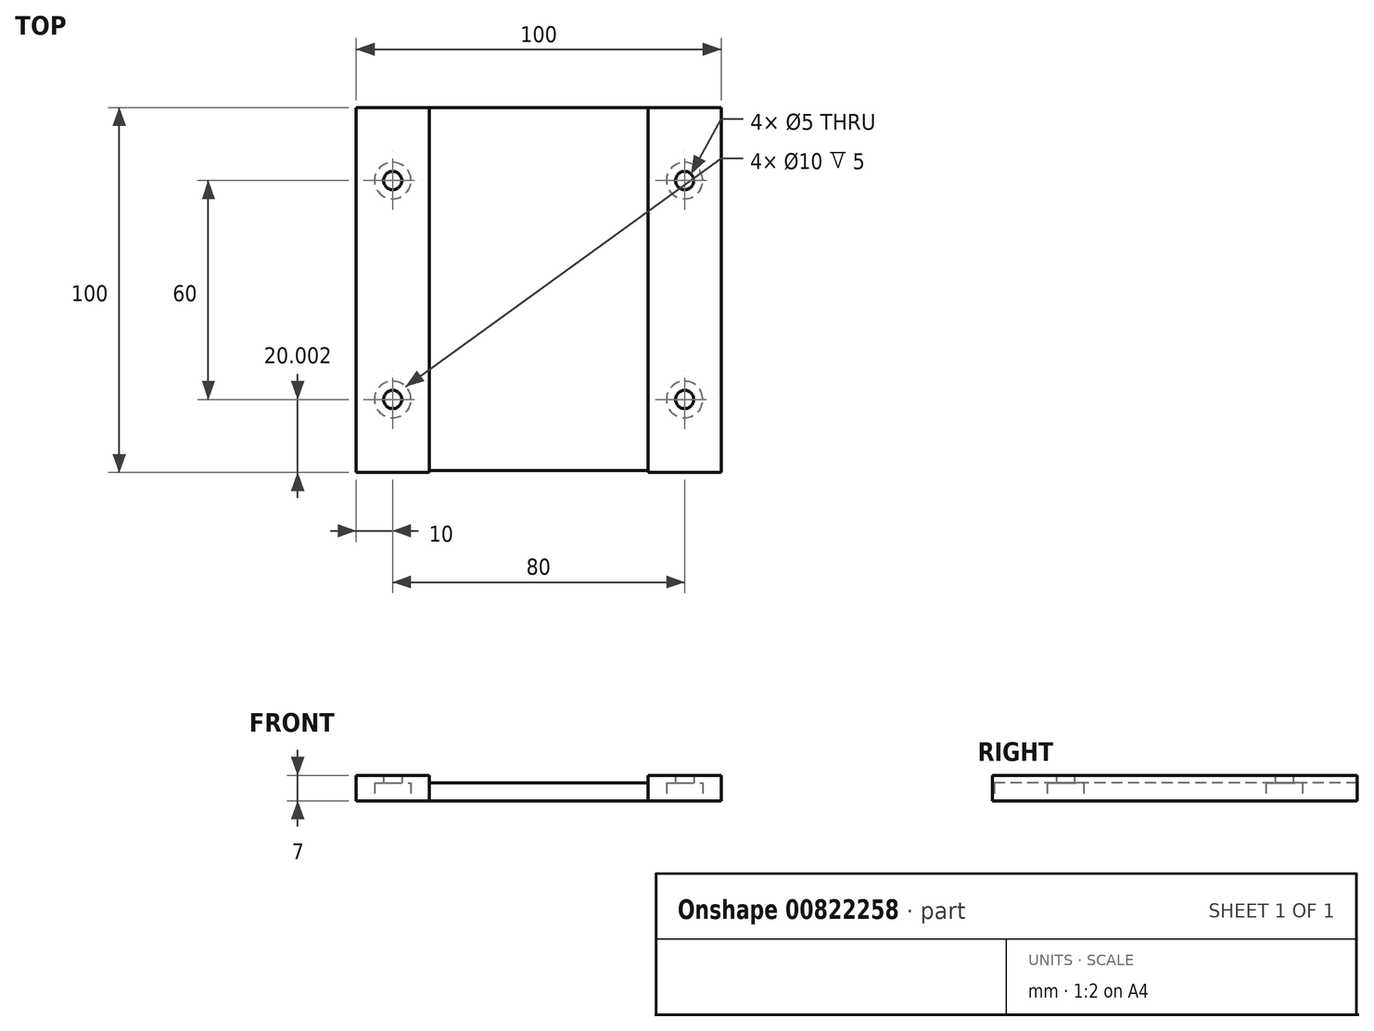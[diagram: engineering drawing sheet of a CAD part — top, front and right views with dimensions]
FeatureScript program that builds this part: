
annotation { "Feature Type Name" : "Feature", "Feature Type Description" : "" }
export const myFeature = defineFeature(function(context is Context, id is Id, definition is map)
    precondition{}
    {
        {
            var Q0;
            Q0=qCreatedBy(makeId("Top.planeOp"),FACE);
            var sketch = newSketch(context, id + "F0", { "sketchPlane" : qUnion([Q0])});
            skLineSegment(sketch, "E0.bottom", {"start": v(-50, 49.93) * mm, "end": v(-30, 49.93) * mm});
            skLineSegment(sketch, "E0.top", {"start": v(-50, -50.07) * mm, "end": v(-30, -50.07) * mm});
            skLineSegment(sketch, "E0.left", {"start": v(-50, 49.93) * mm, "end": v(-50, -50.07) * mm});
            skLineSegment(sketch, "E0.right", {"start": v(-30, 49.93) * mm, "end": v(-30, -50.07) * mm});
            skLineSegment(sketch, "E1.bottom", {"start": v(-30, 49.93) * mm, "end": v(30, 49.93) * mm});
            skLineSegment(sketch, "E1.top", {"start": v(-30, -49.53) * mm, "end": v(30, -49.53) * mm});
            skLineSegment(sketch, "E1.left", {"start": v(-30, 49.93) * mm, "end": v(-30, -49.53) * mm});
            skLineSegment(sketch, "E1.right", {"start": v(30, 49.93) * mm, "end": v(30, -49.53) * mm});
            skLineSegment(sketch, "E2.bottom", {"start": v(30, 49.93) * mm, "end": v(50, 49.93) * mm});
            skLineSegment(sketch, "E2.top", {"start": v(30, -50.07) * mm, "end": v(50, -50.07) * mm});
            skLineSegment(sketch, "E2.left", {"start": v(30, 49.93) * mm, "end": v(30, -50.07) * mm});
            skLineSegment(sketch, "E2.right", {"start": v(50, 49.93) * mm, "end": v(50, -50.07) * mm});
            skPoint(sketch, "E3", {"position": v(-40, 29.93) * mm});
            skPoint(sketch, "E4", {"position": v(-40, -30.07) * mm});
            skPoint(sketch, "E5.MirrorP", {"position": v(40, 29.93) * mm});
            skPoint(sketch, "E6.MirrorP", {"position": v(40, -30.07) * mm});
            skSolve(sketch);
        }
        {
            var Q0;
            {var subQ0=sQuery(id+"F0.wireOp",EDGE,"E1.bottom");Q0=makeQuery(id+"F0.imprint","IMPRINT",FACE,{"disambiguationData":[TD([[makeQuery(id+"F0.imprint","IMPRINT",EDGE,{"derivedFrom":subQ0}),-1.0]])]});}
            extrude(context, id + "F1", {"entities" : qUnion([Q0]), "depth" : 5 * mm, "offsetDistance" : 25 * mm});
        }
        {
            var Q0;
            Q0=makeQuery(id+"F0.imprint","IMPRINT",FACE,{"disambiguationData":[TD([[makeQuery(id+"F0.imprint","IMPRINT",EDGE,{"derivedFrom":sQuery(id+"F0.wireOp",EDGE,"E0.bottom")}),-1.0]])]});
            var Q1;
            {var subQ3=sQuery(id+"F0.wireOp",EDGE,"E2.bottom");Q1=makeQuery(id+"F0.imprint","IMPRINT",FACE,{"disambiguationData":[TD([[makeQuery(id+"F0.imprint","IMPRINT",EDGE,{"derivedFrom":subQ3}),-1.0]])]});}
            extrude(context, id + "F2", {"entities" : qUnion([Q0, Q1]), "operationType" : NewBodyOperationType.ADD, "depth" : 7 * mm, "offsetDistance" : 25 * mm, "hasSecondDirection" : true, "secondDirectionOppositeDirection" : true, "secondDirectionDepth" : 0 * mm});
        }
        {
            var Q0;
            Q0=sQuery(id+"F0.wireOp",VERTEX,"E4");
            var Q1;
            Q1=sQuery(id+"F0.wireOp",VERTEX,"E3");
            var Q2;
            Q2=sQuery(id+"F0.wireOp",VERTEX,"E6.MirrorP");
            var Q3;
            Q3=sQuery(id+"F0.wireOp",VERTEX,"E5.MirrorP");
            var Q4;
            Q4=makeQuery(id+"F1.opExtrude","SWEPT_BODY",BODY,{"disambiguationData":[OSD([sQuery(id+"F0.wireOp",EDGE,"E1.bottom"),sQuery(id+"F0.wireOp",EDGE,"E1.top"),sQuery(id+"F0.wireOp",EDGE,"E1.left"),sQuery(id+"F0.wireOp",EDGE,"E2.left")])]});
            hole(context, id + "F3", {"style" : HoleStyle.C_BORE, "endStyle" : HoleEndStyle.BLIND, "oppositeDirection" : true, "holeDiameter" : 5 * mm, "cBoreDiameter" : 10 * mm, "cBoreDepth" : 5 * mm, "majorDiameter" : 5 * mm, "holeDepth" : 30 * mm, "isTappedThrough" : true, "tappedDepth" : 12 * mm, "tapClearance" : 3, "locations" : qUnion([Q0, Q1, Q2, Q3]), "scope" : qUnion([Q4])});
        }
    });
